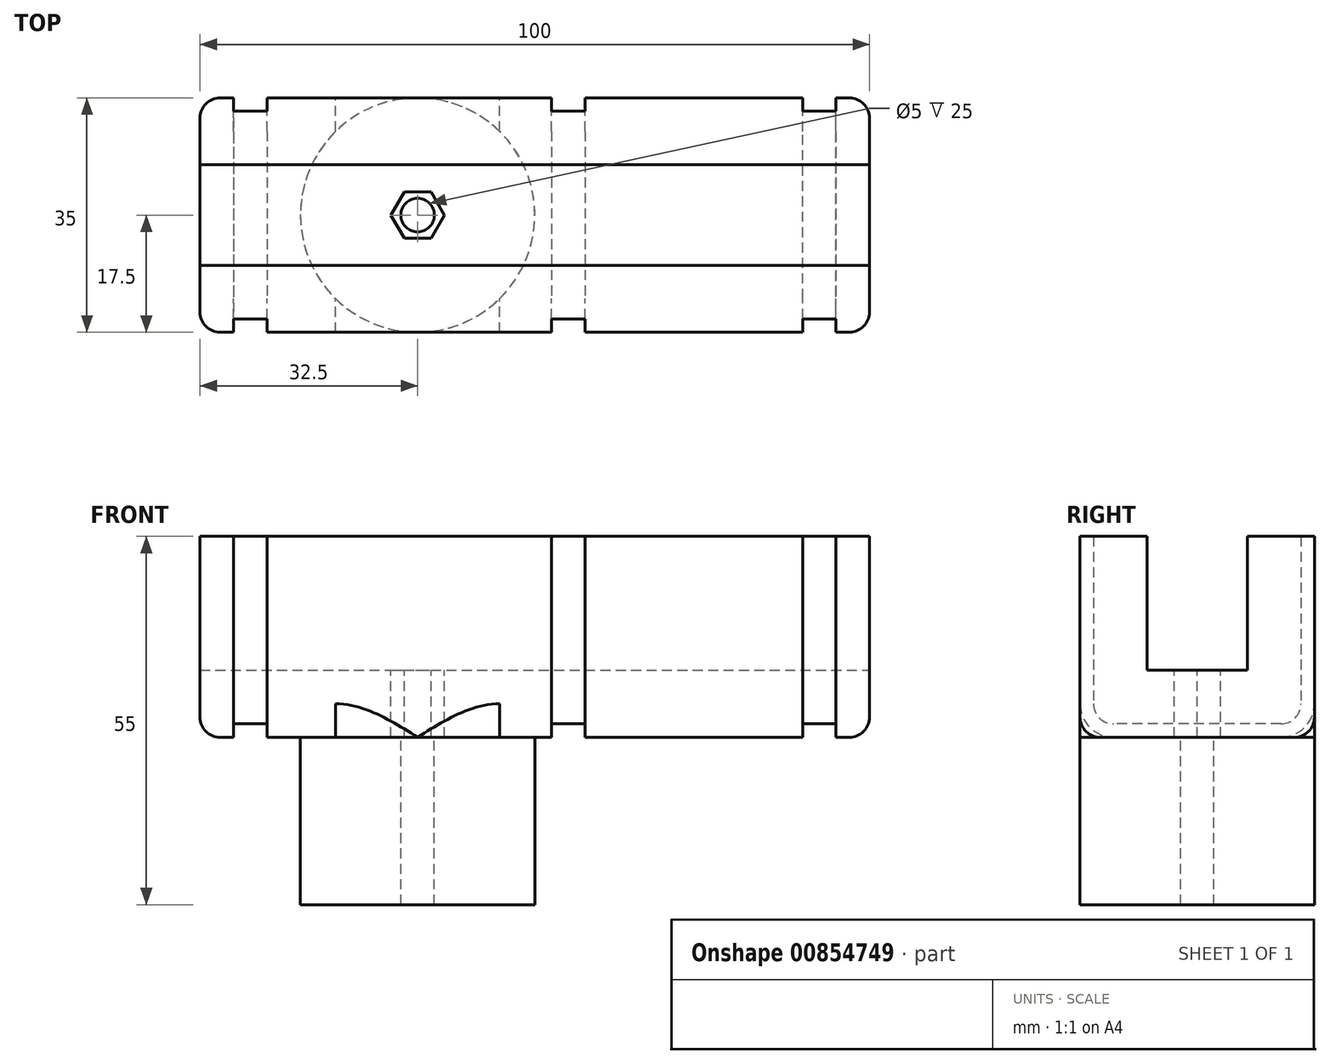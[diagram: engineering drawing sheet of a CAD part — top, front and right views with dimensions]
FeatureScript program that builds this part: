
annotation { "Feature Type Name" : "Feature", "Feature Type Description" : "" }
export const myFeature = defineFeature(function(context is Context, id is Id, definition is map)
    precondition{}
    {
        {
            var Q0;
            Q0=qCreatedBy(makeId("Front.planeOp"),FACE);
            var sketch = newSketch(context, id + "F0", { "sketchPlane" : qUnion([Q0])});
            skLineSegment(sketch, "E0.bottom", {"start": v(50, 15) * mm, "end": v(-50, 15) * mm});
            skLineSegment(sketch, "E0.top", {"start": v(50, -15) * mm, "end": v(-50, -15) * mm});
            skLineSegment(sketch, "E0.left", {"start": v(50, 15) * mm, "end": v(50, -15) * mm});
            skLineSegment(sketch, "E0.right", {"start": v(-50, 15) * mm, "end": v(-50, -15) * mm});
            skPoint(sketch, "E0.middle", {"position": v(0, 0) * mm});
            skLineSegment(sketch, "E1.bottom", {"start": v(-50, 15) * mm, "end": v(50, 15) * mm});
            skLineSegment(sketch, "E1.top", {"start": v(-50, -5) * mm, "end": v(50, -5) * mm});
            skLineSegment(sketch, "E1.left", {"start": v(-50, 15) * mm, "end": v(-50, -5) * mm});
            skLineSegment(sketch, "E1.right", {"start": v(50, 15) * mm, "end": v(50, -5) * mm});
            skSolve(sketch);
        }
        {
            var Q0;
            {var subQ0=sQuery(id+"F0.wireOp",EDGE,"E0.top");Q0=makeQuery(id+"F0.imprint","IMPRINT",FACE,{"disambiguationData":[TD([[makeQuery(id+"F0.imprint","IMPRINT",EDGE,{"derivedFrom":subQ0}),-1.0]])]});}
            var Q1;
            {var subQ0=sQuery(id+"F0.wireOp",EDGE,"E0.bottom");Q1=makeQuery(id+"F0.imprint","IMPRINT",FACE,{"disambiguationData":[TD([[makeQuery(id+"F0.imprint","IMPRINT",EDGE,{"derivedFrom":subQ0}),1.0]])]});}
            extrude(context, id + "F1", {"entities" : qUnion([Q0, Q1]), "endBound" : BoundingType.SYMMETRIC, "depth" : 35 * mm, "offsetDistance" : 25 * mm});
        }
        {
            var Q0;
            {var subQ0=sQuery(id+"F0.wireOp",EDGE,"E0.bottom");Q0=makeQuery(id+"F0.imprint","IMPRINT",FACE,{"disambiguationData":[TD([[makeQuery(id+"F0.imprint","IMPRINT",EDGE,{"derivedFrom":subQ0}),1.0]])]});}
            extrude(context, id + "F2", {"entities" : qUnion([Q0]), "operationType" : NewBodyOperationType.REMOVE, "endBound" : BoundingType.SYMMETRIC, "oppositeDirection" : true, "depth" : 15 * mm, "offsetDistance" : 25 * mm});
        }
        {
            var Q0;
            Q0=makeQuery(id+"F1.opExtrude","SWEPT_FACE",FACE,{"disambiguationData":[OSD([sQuery(id+"F0.wireOp",EDGE,"E0.top")])]});
            var sketch = newSketch(context, id + "F3", { "sketchPlane" : qUnion([Q0])});
            skCircle(sketch, "E2", {"center": v(-17.5, 0) * mm, "radius": 17.5 * mm});
            skPoint(sketch, "E3", {"position": v(-35, 0) * mm});
            skPoint(sketch, "E3.positionSnap0", {"position": v(-50, 0) * mm});
            skPoint(sketch, "E4", {"position": v(-42.5, 0) * mm});
            skLineSegment(sketch, "E5", {"start": v(-17.5, 0) * mm, "end": v(-17.5, 22.7) * mm, "construction": true});
            skPoint(sketch, "E6.MirrorP", {"position": v(7.5, 0) * mm});
            skPoint(sketch, "E7.MirrorP", {"position": v(42.5, 0) * mm});
            skSolve(sketch);
        }
        {
            var Q0;
            Q0=makeQuery(id+"F2.boolean.opBoolean","COPY",FACE,{"derivedFrom":makeQuery(id+"F2.opExtrude","SWEPT_FACE",FACE,{"disambiguationData":[OSD([sQuery(id+"F0.wireOp",EDGE,"E1.top")])]})});
            var sketch = newSketch(context, id + "F4", { "sketchPlane" : qUnion([Q0])});
            skPoint(sketch, "E8.0", {"position": v(-17.5, 0) * mm});
            skCircle(sketch, "E9", {"center": v(-17.5, 0) * mm, "radius": 2.5 * mm});
            skCircle(sketch, "E10.cCircle", {"center": v(-17.5, 0) * mm, "radius": 4 * mm, "construction": true});
            skLineSegment(sketch, "E10.0", {"start": v(-21.5, 0) * mm, "end": v(-19.5, 3.46) * mm});
            skLineSegment(sketch, "E10.1", {"start": v(-19.5, 3.46) * mm, "end": v(-15.5, 3.46) * mm});
            skLineSegment(sketch, "E10.2", {"start": v(-15.5, 3.46) * mm, "end": v(-13.5, 0) * mm});
            skLineSegment(sketch, "E10.3", {"start": v(-13.5, 0) * mm, "end": v(-15.5, -3.46) * mm});
            skLineSegment(sketch, "E10.4", {"start": v(-15.5, -3.46) * mm, "end": v(-19.5, -3.46) * mm});
            skLineSegment(sketch, "E10.5", {"start": v(-19.5, -3.46) * mm, "end": v(-21.5, 0) * mm});
            skSolve(sketch);
        }
        {
            var Q0;
            Q0=makeQuery(id+"F4.imprint","IMPRINT",FACE,{"disambiguationData":[TD([[makeQuery(id+"F4.imprint","IMPRINT",EDGE,{"derivedFrom":sQuery(id+"F4.wireOp",EDGE,"E9")}),-1.0]])]});
            extrude(context, id + "F5", {"entities" : qUnion([Q0]), "operationType" : NewBodyOperationType.REMOVE, "oppositeDirection" : true, "depth" : 10 * mm, "offsetDistance" : 25 * mm});
        }
        {
            var Q0;
            Q0=makeQuery(id+"F4.imprint","IMPRINT",FACE,{"disambiguationData":[TD([[makeQuery(id+"F4.imprint","IMPRINT",EDGE,{"derivedFrom":sQuery(id+"F4.wireOp",EDGE,"E9")}),1.0]])]});
            extrude(context, id + "F6", {"entities" : qUnion([Q0]), "operationType" : NewBodyOperationType.REMOVE, "endBound" : BoundingType.THROUGH_ALL, "oppositeDirection" : true, "depth" : 25 * mm, "offsetDistance" : 25 * mm});
        }
        {
            var Q0;
            {var subQ0=sQuery(id+"F3.wireOp",EDGE,"E2");var subQ1=sQuery(id+"F0.wireOp",EDGE,"E0.top");var subQ2=makeQuery(id+"F3.imprint","INTERSECT",VERTEX,{"derivedFrom":[makeQuery(id+"F1.opExtrude","CAP_EDGE",EDGE,{"disambiguationData":[OSD([subQ1])],"isStart":true}),subQ0]});Q0=makeQuery(id+"F3.imprint","IMPRINT",FACE,{"disambiguationData":[TD([[makeQuery(id+"F3.imprint","IMPRINT",EDGE,{"disambiguationData":[TD([[subQ2,1.0]])],"derivedFrom":subQ0}),1.0]])]});}
            cPlane(context, id + "F7", {"entities" : qUnion([Q0]), "cplaneType" : CPlaneType.OFFSET, "offset" : 90 * mm, "width" : 150 * mm, "height" : 150 * mm});
        }
        {
            var Q0;
            Q0=sQuery(id+"F3.wireOp",VERTEX,"E4");
            var Q1;
            Q1=qCreatedBy(makeId("Right.planeOp"),FACE);
            cPlane(context, id + "F8", {"entities" : qUnion([Q0, Q1]), "cplaneType" : CPlaneType.PLANE_POINT, "offset" : 25 * mm, "width" : 150 * mm, "height" : 150 * mm});
        }
        {
            var Q0;
            Q0=qCreatedBy(id+"F8.planeOp",FACE);
            var sketch = newSketch(context, id + "F9", { "sketchPlane" : qUnion([Q0])});
            skLineSegment(sketch, "E11.0", {"start": v(15.5, 15) * mm, "end": v(15.5, -13) * mm});
            skLineSegment(sketch, "E11.1", {"start": v(15.5, -13) * mm, "end": v(-15.5, -13) * mm});
            skLineSegment(sketch, "E11.2", {"start": v(-15.5, 15) * mm, "end": v(-15.5, -13) * mm});
            skLineSegment(sketch, "E12.0", {"start": v(-17.5, 15) * mm, "end": v(-17.5, -15) * mm});
            skLineSegment(sketch, "E13.0", {"start": v(-17.5, 15) * mm, "end": v(-7.5, 15) * mm});
            skLineSegment(sketch, "E14.0", {"start": v(17.5, -15) * mm, "end": v(-17.5, -15) * mm});
            skLineSegment(sketch, "E15.0", {"start": v(17.5, 15) * mm, "end": v(17.5, -15) * mm});
            skLineSegment(sketch, "E16.0", {"start": v(7.5, 15) * mm, "end": v(17.5, 15) * mm});
            skSolve(sketch);
        }
        {
            var Q0;
            {var subQ2=sQuery(id+"F9.wireOp",EDGE,"E11.0");Q0=makeQuery(id+"F9.imprint","IMPRINT",FACE,{"disambiguationData":[TD([[makeQuery(id+"F9.imprint","IMPRINT",EDGE,{"derivedFrom":subQ2}),1.0]])]});}
            extrude(context, id + "F10", {"entities" : qUnion([Q0]), "operationType" : NewBodyOperationType.REMOVE, "endBound" : BoundingType.SYMMETRIC, "oppositeDirection" : true, "depth" : 5 * mm, "offsetDistance" : 25 * mm});
        }
        {
            var Q0;
            Q0=sQuery(id+"F3.wireOp",VERTEX,"E7.MirrorP");
            var Q1;
            Q1=qCreatedBy(makeId("Right.planeOp"),FACE);
            cPlane(context, id + "F11", {"entities" : qUnion([Q0, Q1]), "cplaneType" : CPlaneType.PLANE_POINT, "offset" : 25 * mm, "width" : 150 * mm, "height" : 150 * mm});
        }
        {
            var Q0;
            Q0=qCreatedBy(makeId("Right.planeOp"),FACE);
            var Q1;
            Q1=sQuery(id+"F3.wireOp",VERTEX,"E6.MirrorP");
            cPlane(context, id + "F12", {"entities" : qUnion([Q0, Q1]), "cplaneType" : CPlaneType.PLANE_POINT, "offset" : 25 * mm, "width" : 150 * mm, "height" : 150 * mm});
        }
        {
            var Q0;
            Q0=qCreatedBy(id+"F11.planeOp",FACE);
            var sketch = newSketch(context, id + "F13", { "sketchPlane" : qUnion([Q0])});
            skLineSegment(sketch, "E17.0", {"start": v(15.5, 15) * mm, "end": v(15.5, -13) * mm});
            skLineSegment(sketch, "E17.1", {"start": v(15.5, -13) * mm, "end": v(-15.5, -13) * mm});
            skLineSegment(sketch, "E17.2", {"start": v(-15.5, 15) * mm, "end": v(-15.5, -13) * mm});
            skLineSegment(sketch, "E18.0", {"start": v(-17.5, 15) * mm, "end": v(-17.5, -15) * mm});
            skLineSegment(sketch, "E19.0", {"start": v(17.5, 15) * mm, "end": v(17.5, -15) * mm});
            skLineSegment(sketch, "E20", {"start": v(-15.5, 15) * mm, "end": v(-17.5, 15) * mm});
            skLineSegment(sketch, "E21", {"start": v(-17.5, -15) * mm, "end": v(17.5, -15) * mm});
            skLineSegment(sketch, "E22", {"start": v(17.5, 15) * mm, "end": v(15.5, 15) * mm});
            skSolve(sketch);
        }
        {
            var Q0;
            Q0=makeQuery(id+"F13.imprint","IMPRINT",FACE,{"disambiguationData":[TD([[makeQuery(id+"F13.imprint","IMPRINT",EDGE,{"derivedFrom":sQuery(id+"F13.wireOp",EDGE,"E17.0")}),1.0]])]});
            extrude(context, id + "F14", {"entities" : qUnion([Q0]), "operationType" : NewBodyOperationType.REMOVE, "endBound" : BoundingType.SYMMETRIC, "oppositeDirection" : true, "depth" : 5 * mm, "offsetDistance" : 25 * mm});
        }
        {
            var Q0;
            Q0=qCreatedBy(id+"F12.planeOp",FACE);
            var sketch = newSketch(context, id + "F15", { "sketchPlane" : qUnion([Q0])});
            skLineSegment(sketch, "E23.0", {"start": v(-15.5, 15) * mm, "end": v(-15.5, -13) * mm});
            skLineSegment(sketch, "E23.1", {"start": v(15.5, -13) * mm, "end": v(-15.5, -13) * mm});
            skLineSegment(sketch, "E23.2", {"start": v(15.5, 15) * mm, "end": v(15.5, -13) * mm});
            skLineSegment(sketch, "E24.0", {"start": v(17.5, 15) * mm, "end": v(17.5, -15) * mm});
            skLineSegment(sketch, "E24.1", {"start": v(17.5, -15) * mm, "end": v(-17.5, -15) * mm});
            skLineSegment(sketch, "E24.2", {"start": v(-17.5, 15) * mm, "end": v(-17.5, -15) * mm});
            skLineSegment(sketch, "E24.3", {"start": v(-17.5, 15) * mm, "end": v(-7.5, 15) * mm});
            skLineSegment(sketch, "E24.4", {"start": v(7.5, 15) * mm, "end": v(17.5, 15) * mm});
            skSolve(sketch);
        }
        {
            var Q0;
            {var subQ2=sQuery(id+"F15.wireOp",EDGE,"E23.0");Q0=makeQuery(id+"F15.imprint","IMPRINT",FACE,{"disambiguationData":[TD([[makeQuery(id+"F15.imprint","IMPRINT",EDGE,{"derivedFrom":subQ2}),-1.0]])]});}
            extrude(context, id + "F16", {"entities" : qUnion([Q0]), "operationType" : NewBodyOperationType.REMOVE, "oppositeDirection" : true, "depth" : 5 * mm, "offsetDistance" : 25 * mm});
        }
        {
            var Q0;
            Q0=makeQuery(id+"F10.boolean.opBoolean","COPY",EDGE,{"derivedFrom":makeQuery(id+"F10.opExtrude","SWEPT_EDGE",EDGE,{"disambiguationData":[OSD([sQuery(id+"F9.wireOp",EDGE,"E11.2"),sQuery(id+"F9.wireOp",EDGE,"E13.0")])]})});
            var Q1;
            Q1=makeQuery(id+"F10.boolean.opBoolean","COPY",EDGE,{"derivedFrom":makeQuery(id+"F10.opExtrude","SWEPT_EDGE",EDGE,{"disambiguationData":[OSD([sQuery(id+"F9.wireOp",EDGE,"E11.0"),sQuery(id+"F9.wireOp",EDGE,"E16.0")])]})});
            var Q2;
            Q2=makeQuery(id+"F10.boolean.opBoolean","COPY",EDGE,{"derivedFrom":makeQuery(id+"F10.opExtrude","SWEPT_EDGE",EDGE,{"disambiguationData":[OSD([sQuery(id+"F9.wireOp",EDGE,"E11.1"),sQuery(id+"F9.wireOp",EDGE,"E11.2")])]})});
            var Q3;
            Q3=makeQuery(id+"F10.boolean.opBoolean","COPY",EDGE,{"derivedFrom":makeQuery(id+"F10.opExtrude","SWEPT_EDGE",EDGE,{"disambiguationData":[OSD([sQuery(id+"F9.wireOp",EDGE,"E11.0"),sQuery(id+"F9.wireOp",EDGE,"E11.1")])]})});
            var Q4;
            Q4=makeQuery(id+"F16.boolean.opBoolean","COPY",EDGE,{"derivedFrom":makeQuery(id+"F16.opExtrude","SWEPT_EDGE",EDGE,{"disambiguationData":[OSD([sQuery(id+"F15.wireOp",EDGE,"E23.0"),sQuery(id+"F15.wireOp",EDGE,"E23.1")])]})});
            var Q5;
            Q5=makeQuery(id+"F16.boolean.opBoolean","COPY",EDGE,{"derivedFrom":makeQuery(id+"F16.opExtrude","SWEPT_EDGE",EDGE,{"disambiguationData":[OSD([sQuery(id+"F15.wireOp",EDGE,"E23.0"),sQuery(id+"F15.wireOp",EDGE,"E24.3")])]})});
            var Q6;
            Q6=makeQuery(id+"F16.boolean.opBoolean","COPY",EDGE,{"derivedFrom":makeQuery(id+"F16.opExtrude","SWEPT_EDGE",EDGE,{"disambiguationData":[OSD([sQuery(id+"F15.wireOp",EDGE,"E23.1"),sQuery(id+"F15.wireOp",EDGE,"E23.2")])]})});
            var Q7;
            Q7=makeQuery(id+"F14.boolean.opBoolean","COPY",EDGE,{"derivedFrom":makeQuery(id+"F14.opExtrude","SWEPT_EDGE",EDGE,{"disambiguationData":[OSD([sQuery(id+"F13.wireOp",EDGE,"E17.0"),sQuery(id+"F13.wireOp",EDGE,"E17.1")])]})});
            var Q8;
            Q8=makeQuery(id+"F14.boolean.opBoolean","COPY",EDGE,{"derivedFrom":makeQuery(id+"F14.opExtrude","SWEPT_EDGE",EDGE,{"disambiguationData":[OSD([sQuery(id+"F13.wireOp",EDGE,"E17.1"),sQuery(id+"F13.wireOp",EDGE,"E17.2")])]})});
            var Q9;
            Q9=makeQuery(id+"F14.boolean.opBoolean","COPY",EDGE,{"derivedFrom":makeQuery(id+"F14.opExtrude","SWEPT_EDGE",EDGE,{"disambiguationData":[OSD([sQuery(id+"F13.wireOp",EDGE,"E17.2"),sQuery(id+"F13.wireOp",EDGE,"E20")])]})});
            var Q10;
            Q10=makeQuery(id+"F14.boolean.opBoolean","COPY",EDGE,{"derivedFrom":makeQuery(id+"F14.opExtrude","SWEPT_EDGE",EDGE,{"disambiguationData":[OSD([sQuery(id+"F13.wireOp",EDGE,"E17.0"),sQuery(id+"F13.wireOp",EDGE,"E22")])]})});
            var Q11;
            Q11=makeQuery(id+"F16.boolean.opBoolean","COPY",EDGE,{"derivedFrom":makeQuery(id+"F16.opExtrude","SWEPT_EDGE",EDGE,{"disambiguationData":[OSD([sQuery(id+"F15.wireOp",EDGE,"E23.2"),sQuery(id+"F15.wireOp",EDGE,"E24.4")])]})});
            fillet(context, id + "F17", {"entities" : qUnion([Q0, Q1, Q2, Q3, Q4, Q5, Q6, Q7, Q8, Q9, Q10, Q11]), "radius" : 3 * mm, "tangentPropagation" : true, "allowEdgeOverflow" : false});
        }
        {
            var Q0;
            {var subQ0=sQuery(id+"F0.wireOp",EDGE,"E0.top");var subQ2=sQuery(id+"F0.wireOp",EDGE,"E1.left");var subQ3=sQuery(id+"F0.wireOp",EDGE,"E0.right");var subQ5=makeQuery(id+"FpHN08Z8G9CQRuu_1.opRevolve","SWEPT_FACE",FACE,{"disambiguationData":[OSD([sQuery(id+"FSq4gacPOnLCIQx_1.wireOp",EDGE,"rNlb3vYY-90e6-qVvO-y8qK-vxR8JLcw6J95")])]});Q0=makeQuery(id+"F10.boolean.opBoolean","SPLIT",EDGE,{"disambiguationData":[TD([subQ5])],"derivedFrom":makeQuery(id+"FpHN08Z8G9CQRuu_1.boolean.opBoolean","SPLIT",EDGE,{"disambiguationData":[TD([makeQuery(id+"F1.opExtrude","SWEPT_FACE",FACE,{"disambiguationData":[OSD([subQ3,subQ2])]})])],"derivedFrom":makeQuery(id+"F1.opExtrude","CAP_EDGE",EDGE,{"disambiguationData":[OSD([subQ0])],"isStart":true})})});}
            var Q1;
            {var subQ0=sQuery(id+"F0.wireOp",EDGE,"E0.top");var subQ2=sQuery(id+"F0.wireOp",EDGE,"E1.right");var subQ3=sQuery(id+"F0.wireOp",EDGE,"E0.left");var subQ5=makeQuery(id+"F14.opExtrude","CAP_FACE",FACE,{"disambiguationData":[OSD([sQuery(id+"F13.wireOp",EDGE,"E17.0"),sQuery(id+"F13.wireOp",EDGE,"E17.1"),sQuery(id+"F13.wireOp",EDGE,"E17.2"),sQuery(id+"F13.wireOp",EDGE,"E18.0"),sQuery(id+"F13.wireOp",EDGE,"E19.0"),sQuery(id+"F13.wireOp",EDGE,"E20"),sQuery(id+"F13.wireOp",EDGE,"E21"),sQuery(id+"F13.wireOp",EDGE,"E22")])],"isStart":false});var subQ6=makeQuery(id+"FpHN08Z8G9CQRuu_1.opRevolve","SWEPT_FACE",FACE,{"disambiguationData":[OSD([sQuery(id+"FSq4gacPOnLCIQx_1.wireOp",EDGE,"rNlb3vYY-90e6-qVvO-y8qK-vxR8JLcw6J95")])]});Q1=makeQuery(id+"F16.boolean.opBoolean","SPLIT",EDGE,{"disambiguationData":[TD([makeQuery(id+"F14.boolean.opBoolean","COPY",FACE,{"derivedFrom":subQ5})])],"derivedFrom":makeQuery(id+"F14.boolean.opBoolean","SPLIT",EDGE,{"disambiguationData":[TD([subQ6])],"derivedFrom":makeQuery(id+"FpHN08Z8G9CQRuu_1.boolean.opBoolean","SPLIT",EDGE,{"disambiguationData":[TD([makeQuery(id+"F1.opExtrude","SWEPT_FACE",FACE,{"disambiguationData":[OSD([subQ3,subQ2])]})])],"derivedFrom":makeQuery(id+"F1.opExtrude","CAP_EDGE",EDGE,{"disambiguationData":[OSD([subQ0])],"isStart":true})})})});}
            var Q2;
            {var subQ0=sQuery(id+"F0.wireOp",EDGE,"E0.left");var subQ1=sQuery(id+"F0.wireOp",EDGE,"E0.top");var subQ4=makeQuery(id+"F1.opExtrude","SWEPT_FACE",FACE,{"disambiguationData":[OSD([subQ0])]});Q2=makeQuery(id+"F14.boolean.opBoolean","SPLIT",EDGE,{"disambiguationData":[TD([subQ4])],"derivedFrom":makeQuery(id+"F10.boolean.opBoolean","SPLIT",EDGE,{"disambiguationData":[TD([subQ4])],"derivedFrom":makeQuery(id+"F1.opExtrude","CAP_EDGE",EDGE,{"disambiguationData":[OSD([subQ1])],"isStart":true})})});}
            var Q3;
            Q3=makeQuery(id+"F1.opExtrude","CAP_EDGE",EDGE,{"disambiguationData":[OSD([sQuery(id+"F0.wireOp",EDGE,"E0.left")])],"isStart":true});
            var Q4;
            Q4=makeQuery(id+"F1.opExtrude","CAP_EDGE",EDGE,{"disambiguationData":[OSD([sQuery(id+"F0.wireOp",EDGE,"E0.left")])],"isStart":false});
            var Q5;
            Q5=makeQuery(id+"F1.opExtrude","SWEPT_EDGE",EDGE,{"disambiguationData":[OSD([sQuery(id+"F0.wireOp",EDGE,"E0.top"),sQuery(id+"F0.wireOp",EDGE,"E0.left")])]});
            var Q6;
            {var subQ0=sQuery(id+"F0.wireOp",EDGE,"E0.top");var subQ2=sQuery(id+"F0.wireOp",EDGE,"E1.right");var subQ3=sQuery(id+"F0.wireOp",EDGE,"E0.left");var subQ5=makeQuery(id+"F14.opExtrude","CAP_FACE",FACE,{"disambiguationData":[OSD([sQuery(id+"F13.wireOp",EDGE,"E17.0"),sQuery(id+"F13.wireOp",EDGE,"E17.1"),sQuery(id+"F13.wireOp",EDGE,"E17.2"),sQuery(id+"F13.wireOp",EDGE,"E18.0"),sQuery(id+"F13.wireOp",EDGE,"E19.0"),sQuery(id+"F13.wireOp",EDGE,"E20"),sQuery(id+"F13.wireOp",EDGE,"E21"),sQuery(id+"F13.wireOp",EDGE,"E22")])],"isStart":false});var subQ6=makeQuery(id+"FpHN08Z8G9CQRuu_1.opRevolve","SWEPT_FACE",FACE,{"disambiguationData":[OSD([sQuery(id+"FSq4gacPOnLCIQx_1.wireOp",EDGE,"rNlb3vYY-90e6-qVvO-y8qK-vxR8JLcw6J95")])]});Q6=makeQuery(id+"F16.boolean.opBoolean","SPLIT",EDGE,{"disambiguationData":[TD([makeQuery(id+"F14.boolean.opBoolean","COPY",FACE,{"derivedFrom":subQ5})])],"derivedFrom":makeQuery(id+"F14.boolean.opBoolean","SPLIT",EDGE,{"disambiguationData":[TD([subQ6])],"derivedFrom":makeQuery(id+"FpHN08Z8G9CQRuu_1.boolean.opBoolean","SPLIT",EDGE,{"disambiguationData":[TD([makeQuery(id+"F1.opExtrude","SWEPT_FACE",FACE,{"disambiguationData":[OSD([subQ3,subQ2])]})])],"derivedFrom":makeQuery(id+"F1.opExtrude","CAP_EDGE",EDGE,{"disambiguationData":[OSD([subQ0])],"isStart":false})})})});}
            var Q7;
            Q7=makeQuery(id+"F1.opExtrude","CAP_EDGE",EDGE,{"disambiguationData":[OSD([sQuery(id+"F0.wireOp",EDGE,"E0.right")])],"isStart":true});
            var Q8;
            {var subQ0=sQuery(id+"F0.wireOp",EDGE,"E0.right");var subQ1=sQuery(id+"F0.wireOp",EDGE,"E0.top");Q8=makeQuery(id+"F10.boolean.opBoolean","SPLIT",EDGE,{"disambiguationData":[TD([makeQuery(id+"F1.opExtrude","SWEPT_FACE",FACE,{"disambiguationData":[OSD([subQ0])]})])],"derivedFrom":makeQuery(id+"F1.opExtrude","CAP_EDGE",EDGE,{"disambiguationData":[OSD([subQ1])],"isStart":true})});}
            var Q9;
            Q9=makeQuery(id+"F1.opExtrude","SWEPT_EDGE",EDGE,{"disambiguationData":[OSD([sQuery(id+"F0.wireOp",EDGE,"E0.top"),sQuery(id+"F0.wireOp",EDGE,"E0.right")])]});
            var Q10;
            Q10=makeQuery(id+"F1.opExtrude","CAP_EDGE",EDGE,{"disambiguationData":[OSD([sQuery(id+"F0.wireOp",EDGE,"E0.right")])],"isStart":false});
            var Q11;
            {var subQ0=sQuery(id+"F0.wireOp",EDGE,"E0.top");var subQ2=sQuery(id+"F0.wireOp",EDGE,"E1.left");var subQ3=sQuery(id+"F0.wireOp",EDGE,"E0.right");var subQ5=makeQuery(id+"FpHN08Z8G9CQRuu_1.opRevolve","SWEPT_FACE",FACE,{"disambiguationData":[OSD([sQuery(id+"FSq4gacPOnLCIQx_1.wireOp",EDGE,"rNlb3vYY-90e6-qVvO-y8qK-vxR8JLcw6J95")])]});Q11=makeQuery(id+"F10.boolean.opBoolean","SPLIT",EDGE,{"disambiguationData":[TD([subQ5])],"derivedFrom":makeQuery(id+"FpHN08Z8G9CQRuu_1.boolean.opBoolean","SPLIT",EDGE,{"disambiguationData":[TD([makeQuery(id+"F1.opExtrude","SWEPT_FACE",FACE,{"disambiguationData":[OSD([subQ3,subQ2])]})])],"derivedFrom":makeQuery(id+"F1.opExtrude","CAP_EDGE",EDGE,{"disambiguationData":[OSD([subQ0])],"isStart":false})})});}
            var Q12;
            {var subQ0=sQuery(id+"F0.wireOp",EDGE,"E0.left");var subQ1=sQuery(id+"F0.wireOp",EDGE,"E0.top");var subQ4=makeQuery(id+"F1.opExtrude","SWEPT_FACE",FACE,{"disambiguationData":[OSD([subQ0])]});Q12=makeQuery(id+"F14.boolean.opBoolean","SPLIT",EDGE,{"disambiguationData":[TD([subQ4])],"derivedFrom":makeQuery(id+"F10.boolean.opBoolean","SPLIT",EDGE,{"disambiguationData":[TD([subQ4])],"derivedFrom":makeQuery(id+"F1.opExtrude","CAP_EDGE",EDGE,{"disambiguationData":[OSD([subQ1])],"isStart":false})})});}
            var Q13;
            {var subQ0=sQuery(id+"F0.wireOp",EDGE,"E0.right");var subQ1=sQuery(id+"F0.wireOp",EDGE,"E0.top");Q13=makeQuery(id+"F10.boolean.opBoolean","SPLIT",EDGE,{"disambiguationData":[TD([makeQuery(id+"F1.opExtrude","SWEPT_FACE",FACE,{"disambiguationData":[OSD([subQ0])]})])],"derivedFrom":makeQuery(id+"F1.opExtrude","CAP_EDGE",EDGE,{"disambiguationData":[OSD([subQ1])],"isStart":false})});}
            fillet(context, id + "F18", {"entities" : qUnion([Q0, Q1, Q2, Q3, Q4, Q5, Q6, Q7, Q8, Q9, Q10, Q11, Q12, Q13]), "radius" : 3 * mm, "tangentPropagation" : true, "allowEdgeOverflow" : false});
        }
        {
            var Q0;
            {var subQ0=sQuery(id+"F3.wireOp",EDGE,"E2");var subQ1=sQuery(id+"F0.wireOp",EDGE,"E0.top");var subQ2=makeQuery(id+"F3.imprint","INTERSECT",VERTEX,{"derivedFrom":[makeQuery(id+"F1.opExtrude","CAP_EDGE",EDGE,{"disambiguationData":[OSD([subQ1])],"isStart":true}),subQ0]});Q0=makeQuery(id+"F3.imprint","IMPRINT",FACE,{"disambiguationData":[TD([[makeQuery(id+"F3.imprint","IMPRINT",EDGE,{"disambiguationData":[TD([[subQ2,1.0]])],"derivedFrom":subQ0}),1.0]])]});}
            extrude(context, id + "F19", {"entities" : qUnion([Q0]), "operationType" : NewBodyOperationType.ADD, "depth" : 25 * mm, "offsetDistance" : 25 * mm});
        }
        {
            var Q0;
            Q0=makeQuery(id+"F4.imprint","IMPRINT",FACE,{"disambiguationData":[TD([[makeQuery(id+"F4.imprint","IMPRINT",EDGE,{"derivedFrom":sQuery(id+"F4.wireOp",EDGE,"E9")}),1.0]])]});
            extrude(context, id + "F20", {"entities" : qUnion([Q0]), "operationType" : NewBodyOperationType.REMOVE, "endBound" : BoundingType.THROUGH_ALL, "oppositeDirection" : true, "depth" : 25 * mm, "offsetDistance" : 25 * mm});
        }
        {
            var Q0;
            {var subQ0=sQuery(id+"F0.wireOp",EDGE,"E0.left");var subQ1=sQuery(id+"F0.wireOp",EDGE,"E0.top");var subQ4=makeQuery(id+"F14.opExtrude","CAP_FACE",FACE,{"disambiguationData":[OSD([sQuery(id+"F13.wireOp",EDGE,"E17.0"),sQuery(id+"F13.wireOp",EDGE,"E17.1"),sQuery(id+"F13.wireOp",EDGE,"E17.2"),sQuery(id+"F13.wireOp",EDGE,"E18.0"),sQuery(id+"F13.wireOp",EDGE,"E19.0"),sQuery(id+"F13.wireOp",EDGE,"E20"),sQuery(id+"F13.wireOp",EDGE,"E21"),sQuery(id+"F13.wireOp",EDGE,"E22")])],"isStart":false});var subQ5=makeQuery(id+"F10.opExtrude","CAP_FACE",FACE,{"disambiguationData":[OSD([sQuery(id+"F9.wireOp",EDGE,"E11.0"),sQuery(id+"F9.wireOp",EDGE,"E11.1"),sQuery(id+"F9.wireOp",EDGE,"E11.2"),sQuery(id+"F9.wireOp",EDGE,"E12.0"),sQuery(id+"F9.wireOp",EDGE,"E13.0"),sQuery(id+"F9.wireOp",EDGE,"E14.0"),sQuery(id+"F9.wireOp",EDGE,"E15.0"),sQuery(id+"F9.wireOp",EDGE,"E16.0")])],"isStart":true});Q0=makeQuery(id+"F16.boolean.opBoolean","SPLIT",EDGE,{"disambiguationData":[TD([makeQuery(id+"F14.boolean.opBoolean","COPY",FACE,{"derivedFrom":subQ4})])],"derivedFrom":makeQuery(id+"F14.boolean.opBoolean","SPLIT",EDGE,{"disambiguationData":[TD([makeQuery(id+"F10.boolean.opBoolean","COPY",FACE,{"derivedFrom":subQ5})])],"derivedFrom":makeQuery(id+"F10.boolean.opBoolean","SPLIT",EDGE,{"disambiguationData":[TD([makeQuery(id+"F1.opExtrude","SWEPT_FACE",FACE,{"disambiguationData":[OSD([subQ0])]})])],"derivedFrom":makeQuery(id+"F1.opExtrude","CAP_EDGE",EDGE,{"disambiguationData":[OSD([subQ1])],"isStart":false})})})});}
            var Q1;
            {var subQ0=sQuery(id+"F0.wireOp",EDGE,"E0.left");var subQ1=sQuery(id+"F0.wireOp",EDGE,"E0.top");var subQ3=makeQuery(id+"F16.opExtrude","CAP_FACE",FACE,{"disambiguationData":[OSD([sQuery(id+"F15.wireOp",EDGE,"E23.0"),sQuery(id+"F15.wireOp",EDGE,"E23.1"),sQuery(id+"F15.wireOp",EDGE,"E23.2"),sQuery(id+"F15.wireOp",EDGE,"E24.0"),sQuery(id+"F15.wireOp",EDGE,"E24.1"),sQuery(id+"F15.wireOp",EDGE,"E24.2"),sQuery(id+"F15.wireOp",EDGE,"E24.3"),sQuery(id+"F15.wireOp",EDGE,"E24.4")])],"isStart":false});var subQ5=makeQuery(id+"F10.opExtrude","CAP_FACE",FACE,{"disambiguationData":[OSD([sQuery(id+"F9.wireOp",EDGE,"E11.0"),sQuery(id+"F9.wireOp",EDGE,"E11.1"),sQuery(id+"F9.wireOp",EDGE,"E11.2"),sQuery(id+"F9.wireOp",EDGE,"E12.0"),sQuery(id+"F9.wireOp",EDGE,"E13.0"),sQuery(id+"F9.wireOp",EDGE,"E14.0"),sQuery(id+"F9.wireOp",EDGE,"E15.0"),sQuery(id+"F9.wireOp",EDGE,"E16.0")])],"isStart":true});var subQ6=makeQuery(id+"F10.boolean.opBoolean","COPY",FACE,{"derivedFrom":subQ5});Q1=makeQuery(id+"F19.boolean.opBoolean","SPLIT",EDGE,{"disambiguationData":[TD([makeQuery(id+"F16.boolean.opBoolean","COPY",FACE,{"derivedFrom":subQ3})])],"derivedFrom":makeQuery(id+"F16.boolean.opBoolean","SPLIT",EDGE,{"disambiguationData":[TD([subQ6])],"derivedFrom":makeQuery(id+"F14.boolean.opBoolean","SPLIT",EDGE,{"disambiguationData":[TD([subQ6])],"derivedFrom":makeQuery(id+"F10.boolean.opBoolean","SPLIT",EDGE,{"disambiguationData":[TD([makeQuery(id+"F1.opExtrude","SWEPT_FACE",FACE,{"disambiguationData":[OSD([subQ0])]})])],"derivedFrom":makeQuery(id+"F1.opExtrude","CAP_EDGE",EDGE,{"disambiguationData":[OSD([subQ1])],"isStart":false})})})})});}
            var Q2;
            {var subQ0=sQuery(id+"F0.wireOp",EDGE,"E0.left");var subQ1=sQuery(id+"F0.wireOp",EDGE,"E0.top");var subQ4=makeQuery(id+"F10.opExtrude","CAP_FACE",FACE,{"disambiguationData":[OSD([sQuery(id+"F9.wireOp",EDGE,"E11.0"),sQuery(id+"F9.wireOp",EDGE,"E11.1"),sQuery(id+"F9.wireOp",EDGE,"E11.2"),sQuery(id+"F9.wireOp",EDGE,"E12.0"),sQuery(id+"F9.wireOp",EDGE,"E13.0"),sQuery(id+"F9.wireOp",EDGE,"E14.0"),sQuery(id+"F9.wireOp",EDGE,"E15.0"),sQuery(id+"F9.wireOp",EDGE,"E16.0")])],"isStart":true});var subQ5=makeQuery(id+"F10.boolean.opBoolean","COPY",FACE,{"derivedFrom":subQ4});Q2=makeQuery(id+"F19.boolean.opBoolean","SPLIT",EDGE,{"disambiguationData":[TD([subQ5])],"derivedFrom":makeQuery(id+"F16.boolean.opBoolean","SPLIT",EDGE,{"disambiguationData":[TD([subQ5])],"derivedFrom":makeQuery(id+"F14.boolean.opBoolean","SPLIT",EDGE,{"disambiguationData":[TD([subQ5])],"derivedFrom":makeQuery(id+"F10.boolean.opBoolean","SPLIT",EDGE,{"disambiguationData":[TD([makeQuery(id+"F1.opExtrude","SWEPT_FACE",FACE,{"disambiguationData":[OSD([subQ0])]})])],"derivedFrom":makeQuery(id+"F1.opExtrude","CAP_EDGE",EDGE,{"disambiguationData":[OSD([subQ1])],"isStart":false})})})})});}
            var Q3;
            {var subQ0=sQuery(id+"F0.wireOp",EDGE,"E0.left");var subQ1=sQuery(id+"F0.wireOp",EDGE,"E0.top");var subQ4=makeQuery(id+"F14.opExtrude","CAP_FACE",FACE,{"disambiguationData":[OSD([sQuery(id+"F13.wireOp",EDGE,"E17.0"),sQuery(id+"F13.wireOp",EDGE,"E17.1"),sQuery(id+"F13.wireOp",EDGE,"E17.2"),sQuery(id+"F13.wireOp",EDGE,"E18.0"),sQuery(id+"F13.wireOp",EDGE,"E19.0"),sQuery(id+"F13.wireOp",EDGE,"E20"),sQuery(id+"F13.wireOp",EDGE,"E21"),sQuery(id+"F13.wireOp",EDGE,"E22")])],"isStart":false});var subQ5=makeQuery(id+"F10.opExtrude","CAP_FACE",FACE,{"disambiguationData":[OSD([sQuery(id+"F9.wireOp",EDGE,"E11.0"),sQuery(id+"F9.wireOp",EDGE,"E11.1"),sQuery(id+"F9.wireOp",EDGE,"E11.2"),sQuery(id+"F9.wireOp",EDGE,"E12.0"),sQuery(id+"F9.wireOp",EDGE,"E13.0"),sQuery(id+"F9.wireOp",EDGE,"E14.0"),sQuery(id+"F9.wireOp",EDGE,"E15.0"),sQuery(id+"F9.wireOp",EDGE,"E16.0")])],"isStart":true});Q3=makeQuery(id+"F16.boolean.opBoolean","SPLIT",EDGE,{"disambiguationData":[TD([makeQuery(id+"F14.boolean.opBoolean","COPY",FACE,{"derivedFrom":subQ4})])],"derivedFrom":makeQuery(id+"F14.boolean.opBoolean","SPLIT",EDGE,{"disambiguationData":[TD([makeQuery(id+"F10.boolean.opBoolean","COPY",FACE,{"derivedFrom":subQ5})])],"derivedFrom":makeQuery(id+"F10.boolean.opBoolean","SPLIT",EDGE,{"disambiguationData":[TD([makeQuery(id+"F1.opExtrude","SWEPT_FACE",FACE,{"disambiguationData":[OSD([subQ0])]})])],"derivedFrom":makeQuery(id+"F1.opExtrude","CAP_EDGE",EDGE,{"disambiguationData":[OSD([subQ1])],"isStart":true})})})});}
            var Q4;
            {var subQ0=sQuery(id+"F0.wireOp",EDGE,"E0.left");var subQ1=sQuery(id+"F0.wireOp",EDGE,"E0.top");var subQ3=makeQuery(id+"F10.opExtrude","CAP_FACE",FACE,{"disambiguationData":[OSD([sQuery(id+"F9.wireOp",EDGE,"E11.0"),sQuery(id+"F9.wireOp",EDGE,"E11.1"),sQuery(id+"F9.wireOp",EDGE,"E11.2"),sQuery(id+"F9.wireOp",EDGE,"E12.0"),sQuery(id+"F9.wireOp",EDGE,"E13.0"),sQuery(id+"F9.wireOp",EDGE,"E14.0"),sQuery(id+"F9.wireOp",EDGE,"E15.0"),sQuery(id+"F9.wireOp",EDGE,"E16.0")])],"isStart":true});var subQ4=makeQuery(id+"F10.boolean.opBoolean","COPY",FACE,{"derivedFrom":subQ3});Q4=makeQuery(id+"F19.boolean.opBoolean","SPLIT",EDGE,{"disambiguationData":[TD([subQ4])],"derivedFrom":makeQuery(id+"F16.boolean.opBoolean","SPLIT",EDGE,{"disambiguationData":[TD([subQ4])],"derivedFrom":makeQuery(id+"F14.boolean.opBoolean","SPLIT",EDGE,{"disambiguationData":[TD([subQ4])],"derivedFrom":makeQuery(id+"F10.boolean.opBoolean","SPLIT",EDGE,{"disambiguationData":[TD([makeQuery(id+"F1.opExtrude","SWEPT_FACE",FACE,{"disambiguationData":[OSD([subQ0])]})])],"derivedFrom":makeQuery(id+"F1.opExtrude","CAP_EDGE",EDGE,{"disambiguationData":[OSD([subQ1])],"isStart":true})})})})});}
            fillet(context, id + "F21", {"entities" : qUnion([Q0, Q1, Q2, Q3, Q4]), "radius" : 5 * mm, "tangentPropagation" : true, "allowEdgeOverflow" : false});
        }
    });
